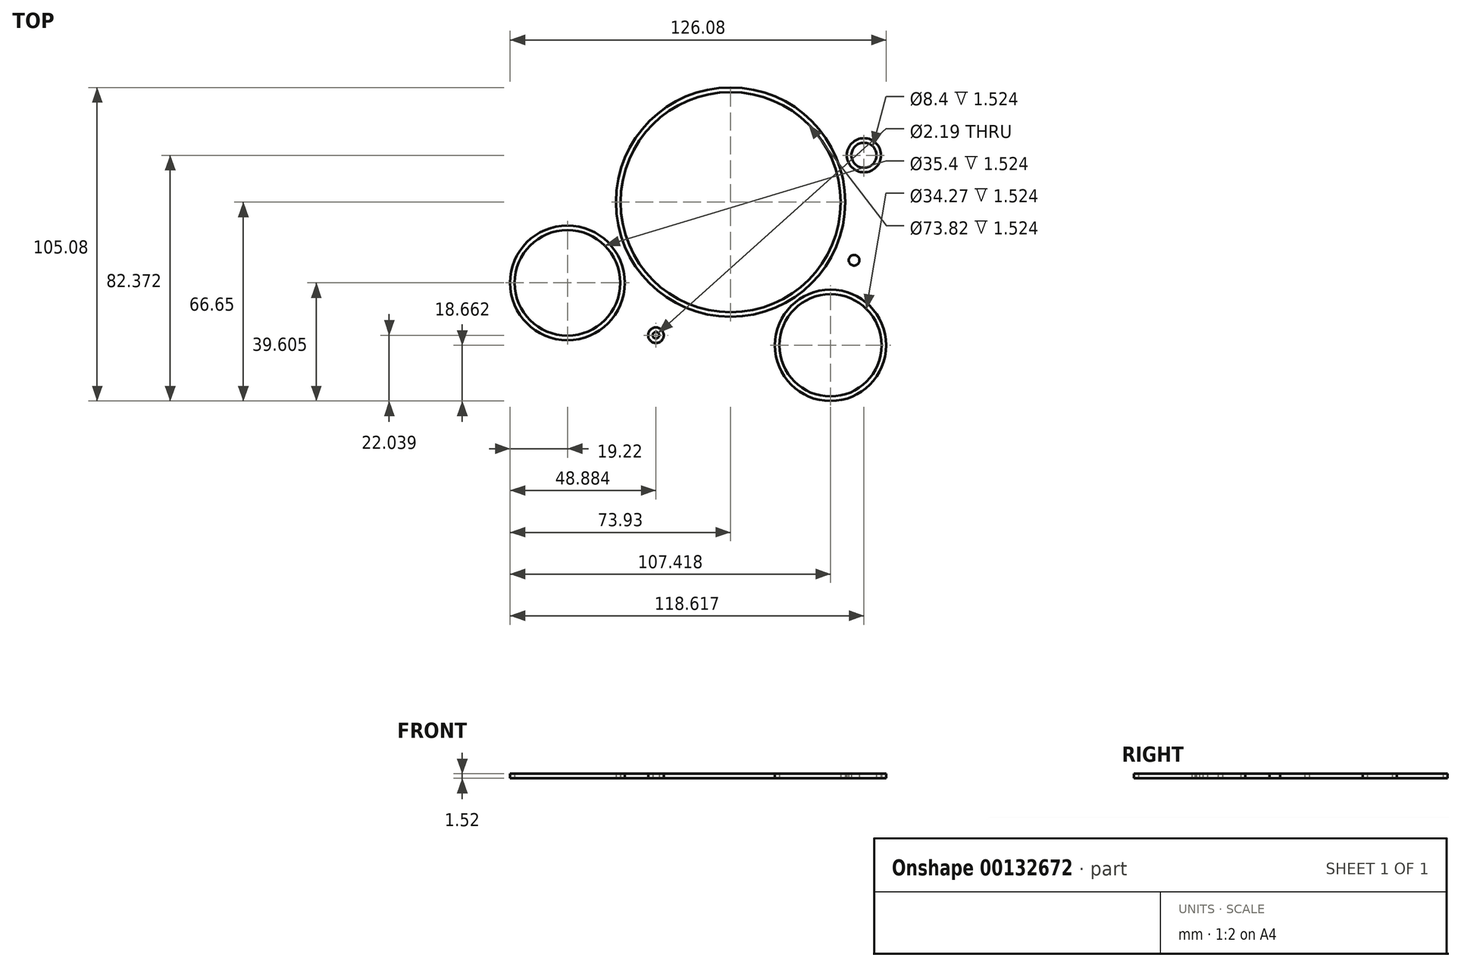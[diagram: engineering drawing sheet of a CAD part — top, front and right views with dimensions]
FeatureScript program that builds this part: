
annotation { "Feature Type Name" : "Feature", "Feature Type Description" : "" }
export const myFeature = defineFeature(function(context is Context, id is Id, definition is map)
    precondition{}
    {
        {
            var Q0;
            Q0=qCreatedBy(makeId("Top.planeOp"),FACE);
            var sketch = newSketch(context, id + "F0", { "sketchPlane" : qUnion([Q0])});
            skCircle(sketch, "E0", {"center": v(33.49, -47.99) * mm, "radius": 17.13 * mm});
            skCircle(sketch, "E1", {"center": v(-25.05, -44.61) * mm, "radius": 2.62 * mm});
            skCircle(sketch, "E2", {"center": v(0, 0) * mm, "radius": 36.9 * mm});
            skCircle(sketch, "E3", {"center": v(44.69, 15.72) * mm, "radius": 5.72 * mm});
            skCircle(sketch, "E4", {"center": v(41.4, -19.47) * mm, "radius": 1.79 * mm});
            skCircle(sketch, "E5", {"center": v(-54.7, -27.04) * mm, "radius": 17.7 * mm});
            skCircle(sketch, "E6.0", {"center": v(0, 0) * mm, "radius": 38.43 * mm});
            skCircle(sketch, "E7.0", {"center": v(-54.7, -27.04) * mm, "radius": 19.22 * mm});
            skCircle(sketch, "E8.0", {"center": v(-25.05, -44.61) * mm, "radius": 1.1 * mm});
            skCircle(sketch, "E9.0", {"center": v(33.49, -47.99) * mm, "radius": 18.66 * mm});
            skCircle(sketch, "E10.0", {"center": v(44.69, 15.72) * mm, "radius": 4.2 * mm});
            skSolve(sketch);
        }
        {
            var Q0;
            Q0 = qSketchRegion(id + "F0", true);
            extrude(context, id + "F1", {"entities" : qUnion([Q0]), "depth" : 1.52 * mm});
        }
    });
